# Revit family: NBS_BetafenceLimited_MtlMeshPnlFncngSym_Securifor4D-Bekasecure
name_source: partatom
category: Site
revit_build: Autodesk Revit 2017 (Build: 20171027_0315(x64)
units: mm (PartAtom-declared; Revit-internal decimal feet)

## family parameters
Cut with Voids When Loaded = No
Part Type = Normal
Round Connector Dimension = Use Diameter
Shared = No

## types (1)
- Securifor 4D + Bekasecure
    Applications = Energy and resources, high security, infra-structure and transport, public spaces and buildings
    AssetType = Fixed
    BIMObjectName = NBS_BetafenceLimited_MetalMeshPanelFencingSystem_Securifor4D-Bekasecure
    Category = Ss_25_14_67_51: Metal mesh panel fencing systems
    Description = Perimeter security
    Diameter = 0 mm  [stored 0 ft]
    DurationUnit = year
    FoundationMaterial = NBS_Concept
    Functionalities = Dissuasion, delay
    Gradient01Maximum = 4.06%
    Gradient01PostAxisDistance = 2823 mm  [stored 9.26181 ft]
    Gradient02Maximum = 8.35%
    Gradient02PostAxisDistance = 2823 mm  [stored 9.26181 ft]
    Gradient03Maximum = 8.35%
    Gradient03PostAxisDistance = 2823 mm  [stored 9.26181 ft]
    Gradient04Maximum = 8.35%
    Gradient04PostAxisDistance = 2823 mm  [stored 9.26181 ft]
    GradientMaximumPostAxisDistance = 2823 mm  [stored 9.26181 ft]
    GradientStep = 3.61%
    Height = 3000 mm  [stored 9.84252 ft]
    IfcExportAs = IfcWallType
    IfcExportType = NOTDEFINED
    IsExternal = Yes
    ManufacturerName = Betafence Limited
    ManufacturerURL = www.betafence.co.uk
    MaximumIncline = 40.00%
    ModelReference = Securifor 4D + Bekasecure
    NBSCertification = www.nationalbimlibrary.com/cert/ioonnjrg
    NBSDescription = Metal mesh panel fencing system
    NBSReference = 25-20-30/145
    Name = MetalMeshPanelFencingSystem_Securifor4D+Bekasecure_BetafenceLimited
    NominalHeight = 3000 mm  [stored 9.84252 ft]
    NominalLength = 0 mm  [stored 0 ft]
    NominalWidth = 2823 mm  [stored 9.26181 ft]
    PanelElevationAboveFoundation = 270 mm  [stored 0.885827 ft]
    PanelHeight = 3000 mm  [stored 9.84252 ft]
    PanelMaterial = NBS_BetafenceLimited_MtlMeshPnlFncngSym_Securifor4D_Panel
    PanelOffsetFromPost = 47 mm  [stored 0.154199 ft]
    PanelOffsetFromPostCL = 7 mm  [stored 0.0229659 ft]
    PanelSizeOptions = 2747 x 1985.2 mm, 2747 x 2442.4 mm, 2520.6 x 3052 mm
    PanelThickness = 9 mm  [stored 0.0295276 ft]
    Panels = Standard mesh
    PostFoundations = Installation guides available on request
    PostHeightAboveGround = 2800 mm  [stored 9.18635 ft]
    PostHeightBelowGround = 200 mm  [stored 0.656168 ft]
    PostMaterial = NBS_Concept
    PostThickness = 155 mm  [stored 0.50853 ft]
    PostWidth = 44 mm  [stored 0.144357 ft]
    Posts = Bekasecure
    ProductInformation = //www.betafence.co.uk/en/securifor-4d-0
    SecurityLevel = High security
    StandardPostAxisDistance = 2823 mm  [stored 9.26181 ft]
    Uniclass2015Code = Ss_25_14_67_51
    Uniclass2015Title = Metal mesh panel fencing systems
    Uniclass2015Version = Systems v1.13
    Version = 2
    WarrantyDurationUnit = year

note: [stored X ft] marks values corroborated as IEEE doubles in the binary element streams (Revit-internal decimal feet)

## geometry (parser evidence)
native form markers: Sweep x7
no freeform markers — native parametric forms only
